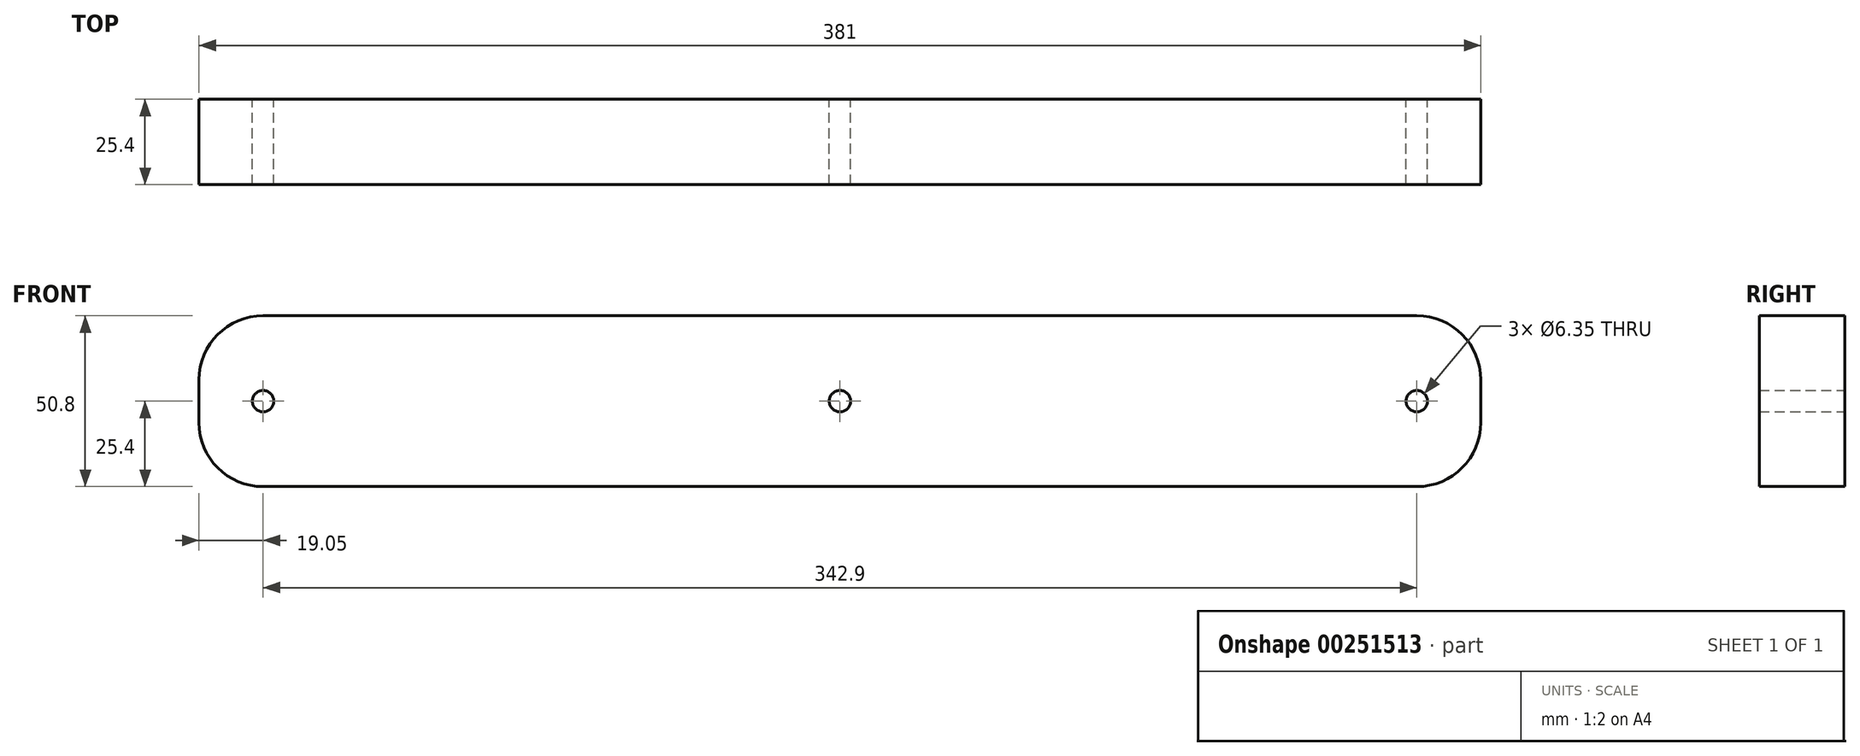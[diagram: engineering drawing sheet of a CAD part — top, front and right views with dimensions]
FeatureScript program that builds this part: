
annotation { "Feature Type Name" : "Feature", "Feature Type Description" : "" }
export const myFeature = defineFeature(function(context is Context, id is Id, definition is map)
    precondition{}
    {
        {
            var Q0;
            Q0=qCreatedBy(makeId("Front.planeOp"),FACE);
            var sketch = newSketch(context, id + "F0", { "sketchPlane" : qUnion([Q0])});
            skLineSegment(sketch, "E0", {"start": v(0, 19.05) * mm, "end": v(0, 31.75) * mm});
            skLineSegment(sketch, "E1", {"start": v(19.05, 50.8) * mm, "end": v(361.95, 50.8) * mm});
            skLineSegment(sketch, "E2", {"start": v(381, 31.75) * mm, "end": v(381, 19.05) * mm});
            skLineSegment(sketch, "E3", {"start": v(361.95, 0) * mm, "end": v(19.05, 0) * mm});
            skPoint(sketch, "E4.visualSharp", {"position": v(0, 50.8) * mm});
            skArc(sketch, "E4.filletArc", {"start": v(19.05, 50.8) * mm, "mid": v(5.58, 45.22) * mm, "end": v(0, 31.75) * mm});
            skPoint(sketch, "E5.visualSharp", {"position": v(0, 0) * mm});
            skArc(sketch, "E5.filletArc", {"start": v(0, 19.05) * mm, "mid": v(5.58, 5.58) * mm, "end": v(19.05, 0) * mm});
            skPoint(sketch, "E6.visualSharp", {"position": v(381, 50.8) * mm});
            skArc(sketch, "E6.filletArc", {"start": v(381, 31.75) * mm, "mid": v(375.42, 45.22) * mm, "end": v(361.95, 50.8) * mm});
            skPoint(sketch, "E7.visualSharp", {"position": v(381, 0) * mm});
            skArc(sketch, "E7.filletArc", {"start": v(361.95, 0) * mm, "mid": v(375.42, 5.58) * mm, "end": v(381, 19.05) * mm});
            skPoint(sketch, "E8.centerSnap0", {"position": v(381, 25.4) * mm});
            skPoint(sketch, "E9.centerSnap0", {"position": v(0, 25.4) * mm});
            skCircle(sketch, "E10", {"center": v(190.5, 25.4) * mm, "radius": 3.18 * mm});
            skPoint(sketch, "E11", {"position": v(190.5, 50.8) * mm});
            skCircle(sketch, "E12", {"center": v(361.95, 25.4) * mm, "radius": 3.18 * mm});
            skCircle(sketch, "E13", {"center": v(19.05, 25.4) * mm, "radius": 3.18 * mm});
            skSolve(sketch);
        }
        {
            var Q0;
            Q0=makeQuery(id+"F0.imprint","IMPRINT",FACE,{"disambiguationData":[TD([[makeQuery(id+"F0.imprint","IMPRINT",EDGE,{"derivedFrom":sQuery(id+"F0.wireOp",EDGE,"E0")}),-1.0]])]});
            extrude(context, id + "F1", {"entities" : qUnion([Q0]), "depth" : 25.4 * mm});
        }
    });
